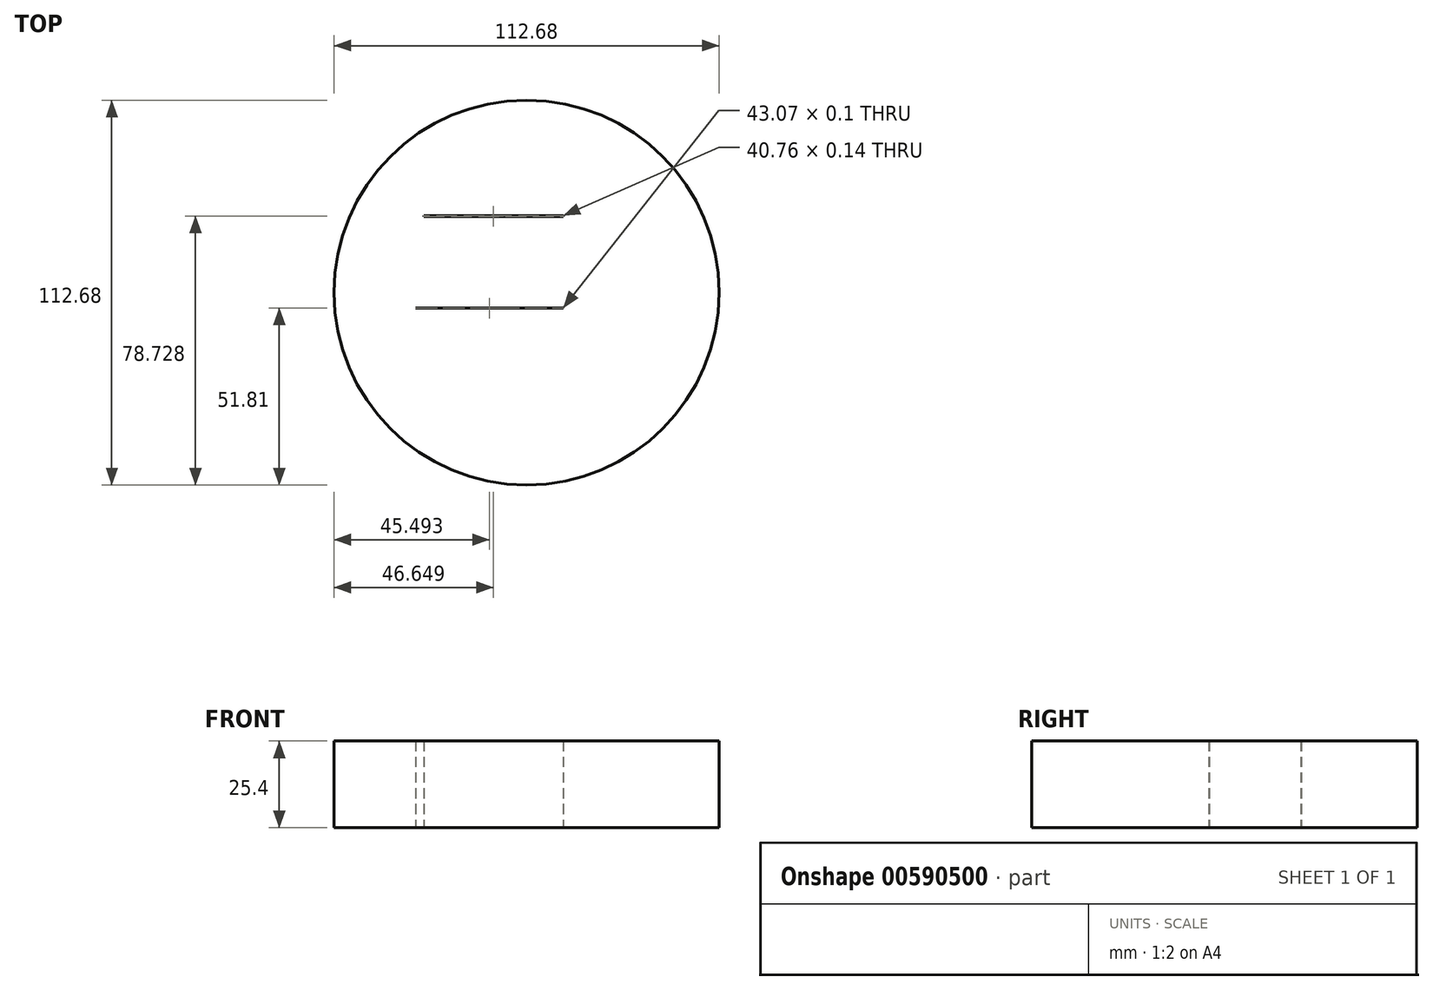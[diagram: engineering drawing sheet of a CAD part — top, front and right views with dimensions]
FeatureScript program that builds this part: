
annotation { "Feature Type Name" : "Feature", "Feature Type Description" : "" }
export const myFeature = defineFeature(function(context is Context, id is Id, definition is map)
    precondition{}
    {
        {
            var Q0;
            Q0=qCreatedBy(makeId("Top.planeOp"),FACE);
            var sketch = newSketch(context, id + "F0", { "sketchPlane" : qUnion([Q0])});
            skCircle(sketch, "E0", {"center": v(-24.53, 10.62) * mm, "radius": 56.34 * mm});
            skLineSegment(sketch, "E1.bottom", {"start": v(-54.6, 32.94) * mm, "end": v(-13.84, 32.94) * mm});
            skLineSegment(sketch, "E1.top", {"start": v(-54.6, 33.08) * mm, "end": v(-13.84, 33.08) * mm});
            skLineSegment(sketch, "E1.left", {"start": v(-54.6, 32.94) * mm, "end": v(-54.6, 33.08) * mm});
            skLineSegment(sketch, "E1.right", {"start": v(-13.84, 32.94) * mm, "end": v(-13.84, 33.08) * mm});
            skLineSegment(sketch, "E2.bottom", {"start": v(-56.91, 6.04) * mm, "end": v(-13.84, 6.04) * mm});
            skLineSegment(sketch, "E2.top", {"start": v(-56.91, 6.14) * mm, "end": v(-13.84, 6.14) * mm});
            skLineSegment(sketch, "E2.left", {"start": v(-56.91, 6.04) * mm, "end": v(-56.91, 6.14) * mm});
            skLineSegment(sketch, "E2.right", {"start": v(-13.84, 6.04) * mm, "end": v(-13.84, 6.14) * mm});
            skArc(sketch, "E3", {"start": v(0, -13.08) * mm, "mid": v(18.58, 13.67) * mm, "end": v(3.23, 42.4) * mm});
            skSolve(sketch);
        }
        {
            var Q0;
            Q0 = qSketchRegion(id + "F0", true);
            extrude(context, id + "F1", {"entities" : qUnion([Q0]), "depth" : 25.4 * mm, "offsetDistance" : 25.4 * mm});
        }
    });
